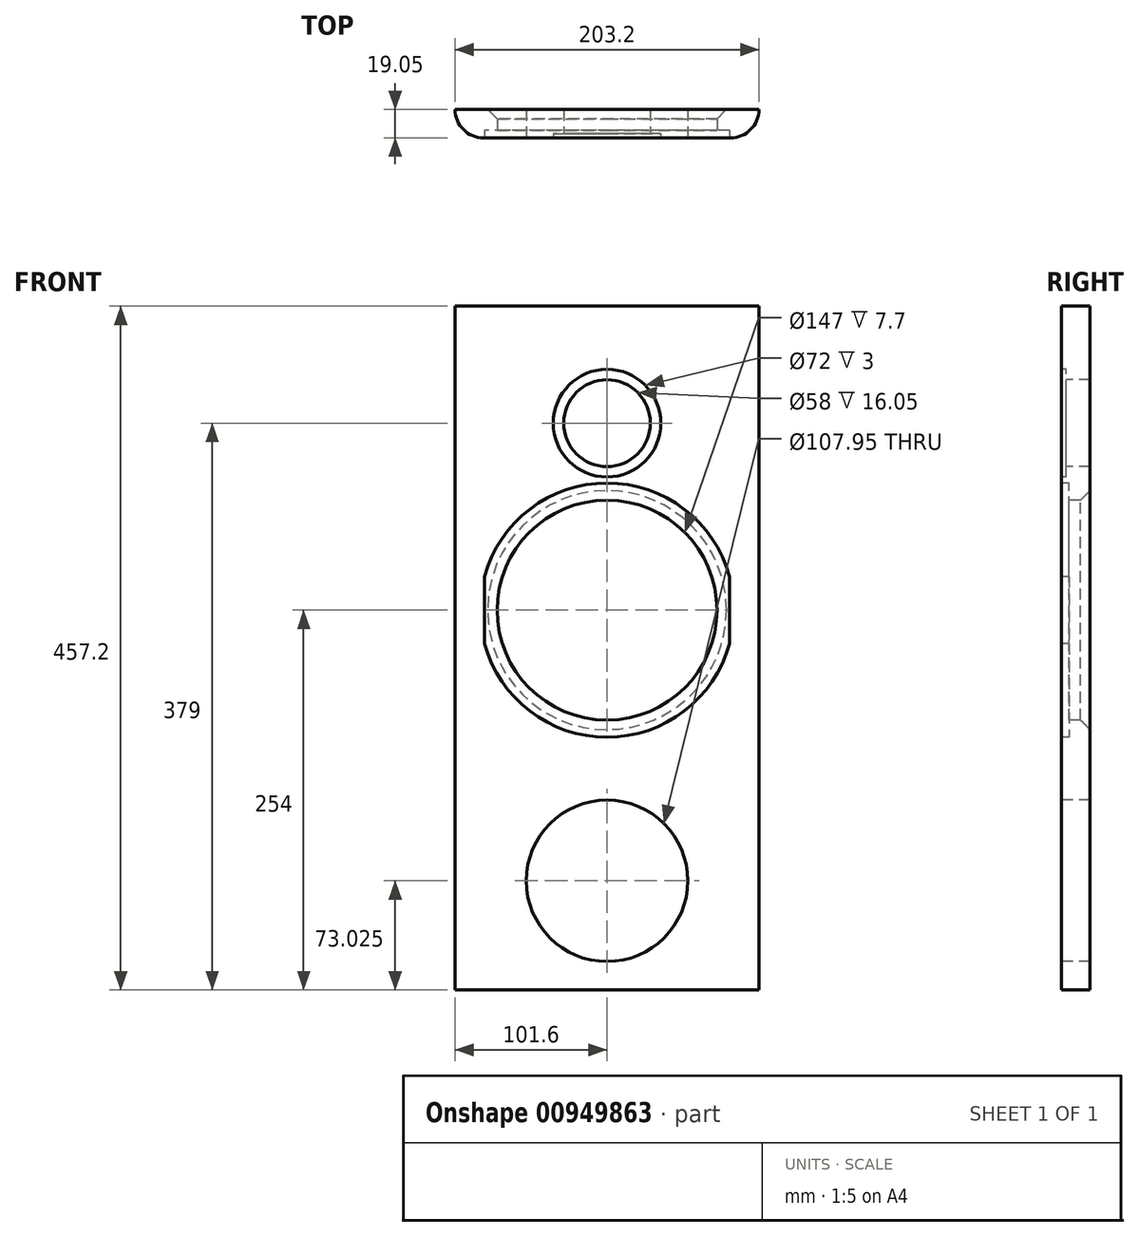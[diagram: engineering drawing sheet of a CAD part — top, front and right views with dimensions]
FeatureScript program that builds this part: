
annotation { "Feature Type Name" : "Feature", "Feature Type Description" : "" }
export const myFeature = defineFeature(function(context is Context, id is Id, definition is map)
    precondition{}
    {
        {
            var Q0;
            Q0=qCreatedBy(makeId("Front.planeOp"),FACE);
            var sketch = newSketch(context, id + "F0", { "sketchPlane" : qUnion([Q0])});
            skLineSegment(sketch, "E0.bottom", {"start": v(101.6, -228.6) * mm, "end": v(-101.6, -228.6) * mm});
            skLineSegment(sketch, "E0.top", {"start": v(101.6, 228.6) * mm, "end": v(-101.6, 228.6) * mm});
            skLineSegment(sketch, "E0.left", {"start": v(101.6, -228.6) * mm, "end": v(101.6, 228.6) * mm});
            skLineSegment(sketch, "E0.right", {"start": v(-101.6, -228.6) * mm, "end": v(-101.6, 228.6) * mm});
            skPoint(sketch, "E0.middle", {"position": v(0, 0) * mm});
            skSolve(sketch);
        }
        {
            var Q0;
            Q0 = qSketchRegion(id + "F0", true);
            extrude(context, id + "F1", {"entities" : qUnion([Q0]), "depth" : 19.05 * mm, "offsetDistance" : 25.4 * mm});
        }
        {
            var Q0;
            Q0=makeQuery(id+"F1.opExtrude","CAP_EDGE",EDGE,{"disambiguationData":[OSD([sQuery(id+"F0.wireOp",EDGE,"E0.right")])],"isStart":false});
            fillet(context, id + "F2", {"entities" : qUnion([Q0]), "radius" : 19.05 * mm, "tangentPropagation" : true, "allowEdgeOverflow" : false});
        }
        {
            var Q0;
            Q0=makeQuery(id+"F1.opExtrude","CAP_EDGE",EDGE,{"disambiguationData":[OSD([sQuery(id+"F0.wireOp",EDGE,"E0.left")])],"isStart":false});
            fillet(context, id + "F3", {"entities" : qUnion([Q0]), "radius" : 19.05 * mm, "tangentPropagation" : true, "allowEdgeOverflow" : false});
        }
        {
            var Q0;
            Q0=makeQuery(id+"F1.opExtrude","CAP_FACE",FACE,{"disambiguationData":[OSD([sQuery(id+"F0.wireOp",EDGE,"E0.bottom"),sQuery(id+"F0.wireOp",EDGE,"E0.top"),sQuery(id+"F0.wireOp",EDGE,"E0.left"),sQuery(id+"F0.wireOp",EDGE,"E0.right")])],"isStart":false});
            var sketch = newSketch(context, id + "F4", { "sketchPlane" : qUnion([Q0])});
            skLineSegment(sketch, "E1", {"start": v(0, 228.6) * mm, "end": v(0, -228.6) * mm, "construction": true});
            skLineSegment(sketch, "E2", {"start": v(-82.55, 25.4) * mm, "end": v(82.55, 25.4) * mm, "construction": true});
            skArc(sketch, "E3", {"start": v(82, 47.78) * mm, "mid": v(0, 110.4) * mm, "end": v(-82, 47.78) * mm});
            skLineSegment(sketch, "E4", {"start": v(82, 47.78) * mm, "end": v(82, 3.02) * mm});
            skLineSegment(sketch, "E5", {"start": v(-82, 47.78) * mm, "end": v(-82, 3.02) * mm});
            skArc(sketch, "E6.trimOffspring", {"start": v(-82, 3.02) * mm, "mid": v(0, -59.6) * mm, "end": v(82, 3.02) * mm});
            skSolve(sketch);
        }
        {
            var Q0;
            Q0 = qSketchRegion(id + "F4", true);
            extrude(context, id + "F5", {"entities" : qUnion([Q0]), "operationType" : NewBodyOperationType.REMOVE, "oppositeDirection" : true, "depth" : 5 * mm, "offsetDistance" : 25.4 * mm});
        }
        {
            var Q0;
            Q0=makeQuery(id+"F4.imprint","IMPRINT",FACE,{"disambiguationData":[TD([[makeQuery(id+"F4.imprint","IMPRINT",EDGE,{"derivedFrom":sQuery(id+"F4.wireOp",EDGE,"E3")}),1.0]])]});
            var sketch = newSketch(context, id + "F6", { "sketchPlane" : qUnion([Q0])});
            skLineSegment(sketch, "E7", {"start": v(-82.98, 25.4) * mm, "end": v(82.16, 25.4) * mm, "construction": true});
            skLineSegment(sketch, "E8", {"start": v(0, -165.76) * mm, "end": v(0, 167.14) * mm, "construction": true});
            skCircle(sketch, "E9", {"center": v(0, 25.4) * mm, "radius": 73.5 * mm});
            skSolve(sketch);
        }
        {
            var Q0;
            Q0 = qSketchRegion(id + "F6", true);
            extrude(context, id + "F7", {"entities" : qUnion([Q0]), "operationType" : NewBodyOperationType.REMOVE, "oppositeDirection" : true, "depth" : 25.4 * mm, "offsetDistance" : 25.4 * mm});
        }
        {
            var Q0;
            Q0=makeQuery(id+"F7.boolean.opBoolean","INTERSECT",EDGE,{"derivedFrom":[makeQuery(id+"F1.opExtrude","CAP_FACE",FACE,{"disambiguationData":[OSD([sQuery(id+"F0.wireOp",EDGE,"E0.bottom"),sQuery(id+"F0.wireOp",EDGE,"E0.top"),sQuery(id+"F0.wireOp",EDGE,"E0.left"),sQuery(id+"F0.wireOp",EDGE,"E0.right")])],"isStart":true}),makeQuery(id+"F7.opExtrude","SWEPT_FACE",FACE,{"disambiguationData":[OSD([sQuery(id+"F6.wireOp",EDGE,"E9")])]})]});
            chamfer(context, id + "F8", {"entities" : qUnion([Q0]), "width" : 6.35 * mm, "tangentPropagation" : true});
        }
        {
            var Q0;
            Q0=makeQuery(id+"F1.opExtrude","CAP_FACE",FACE,{"disambiguationData":[OSD([sQuery(id+"F0.wireOp",EDGE,"E0.bottom"),sQuery(id+"F0.wireOp",EDGE,"E0.top"),sQuery(id+"F0.wireOp",EDGE,"E0.left"),sQuery(id+"F0.wireOp",EDGE,"E0.right")])],"isStart":false});
            var sketch = newSketch(context, id + "F9", { "sketchPlane" : qUnion([Q0])});
            skLineSegment(sketch, "E10", {"start": v(-82.55, 150.4) * mm, "end": v(82.55, 150.4) * mm, "construction": true});
            skCircle(sketch, "E11", {"center": v(0, 150.4) * mm, "radius": 36 * mm});
            skSolve(sketch);
        }
        {
            var Q0;
            Q0 = qSketchRegion(id + "F9", true);
            extrude(context, id + "F10", {"entities" : qUnion([Q0]), "operationType" : NewBodyOperationType.REMOVE, "oppositeDirection" : true, "depth" : 3 * mm, "offsetDistance" : 25.4 * mm});
        }
        {
            var Q0;
            Q0=makeQuery(id+"F1.opExtrude","CAP_FACE",FACE,{"disambiguationData":[OSD([sQuery(id+"F0.wireOp",EDGE,"E0.bottom"),sQuery(id+"F0.wireOp",EDGE,"E0.top"),sQuery(id+"F0.wireOp",EDGE,"E0.left"),sQuery(id+"F0.wireOp",EDGE,"E0.right")])],"isStart":false});
            var sketch = newSketch(context, id + "F11", { "sketchPlane" : qUnion([Q0])});
            skLineSegment(sketch, "E12", {"start": v(0, 228.6) * mm, "end": v(0, -228.6) * mm, "construction": true});
            skLineSegment(sketch, "E13", {"start": v(-82.55, 150.4) * mm, "end": v(82.55, 150.4) * mm, "construction": true});
            skCircle(sketch, "E14", {"center": v(0, 150.4) * mm, "radius": 29 * mm});
            skSolve(sketch);
        }
        {
            var Q0;
            Q0 = qSketchRegion(id + "F11", true);
            extrude(context, id + "F12", {"entities" : qUnion([Q0]), "operationType" : NewBodyOperationType.REMOVE, "oppositeDirection" : true, "depth" : 25.4 * mm, "offsetDistance" : 25.4 * mm});
        }
        {
            var Q0;
            Q0=makeQuery(id+"F1.opExtrude","CAP_FACE",FACE,{"disambiguationData":[OSD([sQuery(id+"F0.wireOp",EDGE,"E0.bottom"),sQuery(id+"F0.wireOp",EDGE,"E0.top"),sQuery(id+"F0.wireOp",EDGE,"E0.left"),sQuery(id+"F0.wireOp",EDGE,"E0.right")])],"isStart":false});
            var sketch = newSketch(context, id + "F13", { "sketchPlane" : qUnion([Q0])});
            skLineSegment(sketch, "E15", {"start": v(0, -228.6) * mm, "end": v(0, 228.6) * mm, "construction": true});
            skLineSegment(sketch, "E16", {"start": v(-82.55, -155.58) * mm, "end": v(82.55, -155.57) * mm, "construction": true});
            skCircle(sketch, "E17", {"center": v(0, -155.58) * mm, "radius": 53.98 * mm});
            skSolve(sketch);
        }
        {
            var Q0;
            Q0 = qSketchRegion(id + "F13", true);
            extrude(context, id + "F14", {"entities" : qUnion([Q0]), "operationType" : NewBodyOperationType.REMOVE, "oppositeDirection" : true, "depth" : 25.4 * mm, "offsetDistance" : 25.4 * mm});
        }
    });
